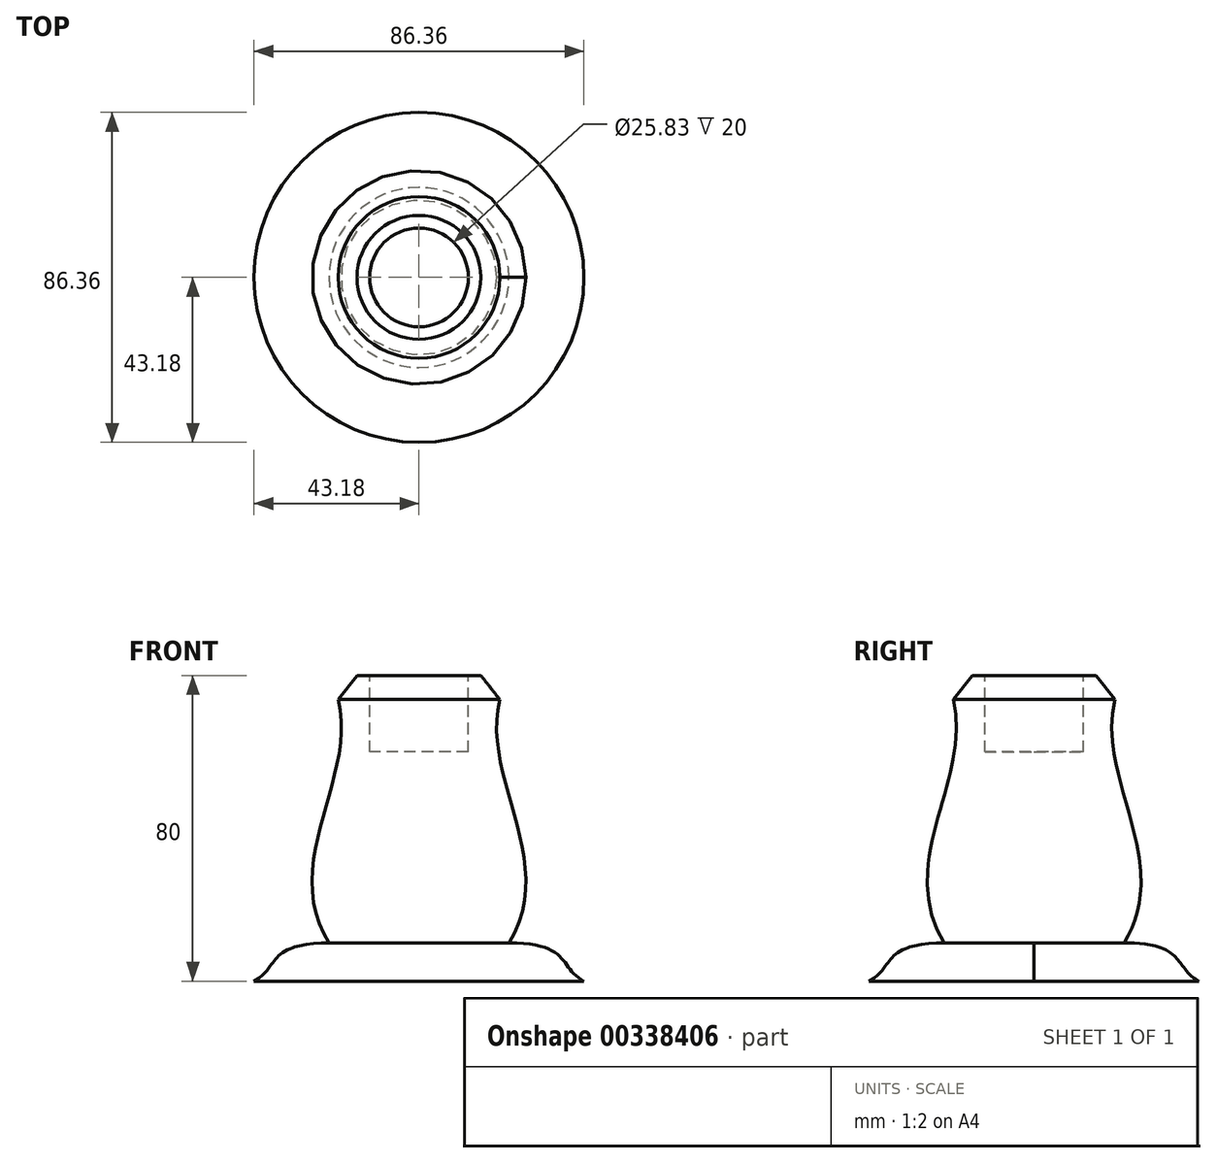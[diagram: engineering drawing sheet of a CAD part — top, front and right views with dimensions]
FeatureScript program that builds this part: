
annotation { "Feature Type Name" : "Feature", "Feature Type Description" : "" }
export const myFeature = defineFeature(function(context is Context, id is Id, definition is map)
    precondition{}
    {
        {
            var Q0;
            Q0=qCreatedBy(makeId("Front.planeOp"),FACE);
            var sketch = newSketch(context, id + "F0", { "sketchPlane" : qUnion([Q0])});
            skLineSegment(sketch, "E0.bottom", {"start": v(11.78, 22.76) * mm, "end": v(23.55, 22.76) * mm});
            skLineSegment(sketch, "E0.left", {"start": v(0, 22.76) * mm, "end": v(0, -47.24) * mm});
            skLineSegment(sketch, "E1.top", {"start": v(0, -57.24) * mm, "end": v(43.18, -57.24) * mm});
            skLineSegment(sketch, "E1.left", {"start": v(0, -47.24) * mm, "end": v(0, -57.24) * mm});
            skFitSpline(sketch, "E2", {"points": [v(23.55, -47.24) * mm, v(43.18, -57.24) * mm], "startDerivative": vector(49.36, 0) * mm, "endDerivative": vector(19.63, -10) * mm});
            skFitSpline(sketch, "E3", {"points": [v(23.55, 22.76) * mm, v(23.55, -47.24) * mm], "startDerivative": vector(-36.12, -68.27) * mm, "endDerivative": vector(-43.32, -70.93) * mm});
            skLineSegment(sketch, "E4", {"start": v(0, 22.76) * mm, "end": v(14.4, 22.76) * mm});
            skPoint(sketch, "E5.bottom.start.orphan", {"position": v(0, 34.54) * mm});
            skSolve(sketch);
        }
        {
            var Q0;
            Q0=makeQuery(id+"F0.imprint","IMPRINT",FACE,{"disambiguationData":[TD([[makeQuery(id+"F0.imprint","IMPRINT",EDGE,{"derivedFrom":sQuery(id+"F0.wireOp",EDGE,"E0.bottom")}),-1.0]])]});
            var Q1;
            Q1=sQuery(id+"F0.wireOp",EDGE,"E0.left");
            revolve(context, id + "F1", {"entities" : qUnion([Q0]), "axis" : qUnion([Q1]), "revolveType" : RevolveType.FULL});
        }
        {
            var Q0;
            Q0=makeQuery(id+"F1.opRevolve","SWEPT_EDGE",EDGE,{"disambiguationData":[OSD([sQuery(id+"F0.wireOp",EDGE,"E0.bottom"),sQuery(id+"F0.wireOp",EDGE,"E3")])]});
            chamfer(context, id + "F2", {"entities" : qUnion([Q0]), "width" : 5.08 * mm, "tangentPropagation" : true});
        }
        {
            var Q0;
            Q0=makeQuery(id+"F1.opRevolve","SWEPT_FACE",FACE,{"disambiguationData":[OSD([sQuery(id+"F0.wireOp",EDGE,"E0.bottom"),sQuery(id+"F0.wireOp",EDGE,"E4")])]});
            var sketch = newSketch(context, id + "F3", { "sketchPlane" : qUnion([Q0])});
            skCircle(sketch, "E6", {"center": v(0, 0) * mm, "radius": 12.92 * mm});
            skSolve(sketch);
        }
        {
            var Q0;
            Q0=makeQuery(id+"F3.imprint","IMPRINT",FACE,{"disambiguationData":[TD([[makeQuery(id+"F3.imprint","IMPRINT",EDGE,{"derivedFrom":sQuery(id+"F3.wireOp",EDGE,"E6")}),1.0]])]});
            extrude(context, id + "F4", {"entities" : qUnion([Q0]), "operationType" : NewBodyOperationType.REMOVE, "oppositeDirection" : true, "depth" : 20 * mm});
        }
    });
